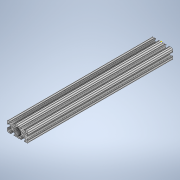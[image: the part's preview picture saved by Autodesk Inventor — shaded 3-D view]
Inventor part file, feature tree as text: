
AUTODESK INVENTOR PART (.ipt)
format: ipt  version: 2020 (Build 240168000, 168)  size: 333,824 bytes
history: native  units: in
note: dims shown in document units (in); Inventor stores cm internally (conversion verified against a paired STEP export)
features: sketch x2, extrude x1
ambient origin geometry x8: Origin, YZ Plane, XZ Plane, XY Plane, X Axis, Y Axis, Z Axis, Center Point
bodies: Solid1 (feature_tree)
feature tree (3):
  extrude  "Extrusion1"  [1 undecoded]
  sketch  "Sketch2"
  sketch  "Sketch1"  dims[d0=14.0in d1=0.0in]
note: 1 required parameter value undecoded (feature->parameter linkage not recoverable at this tier; creation-order binding heuristic only, values carry confidence <= 0.55)
